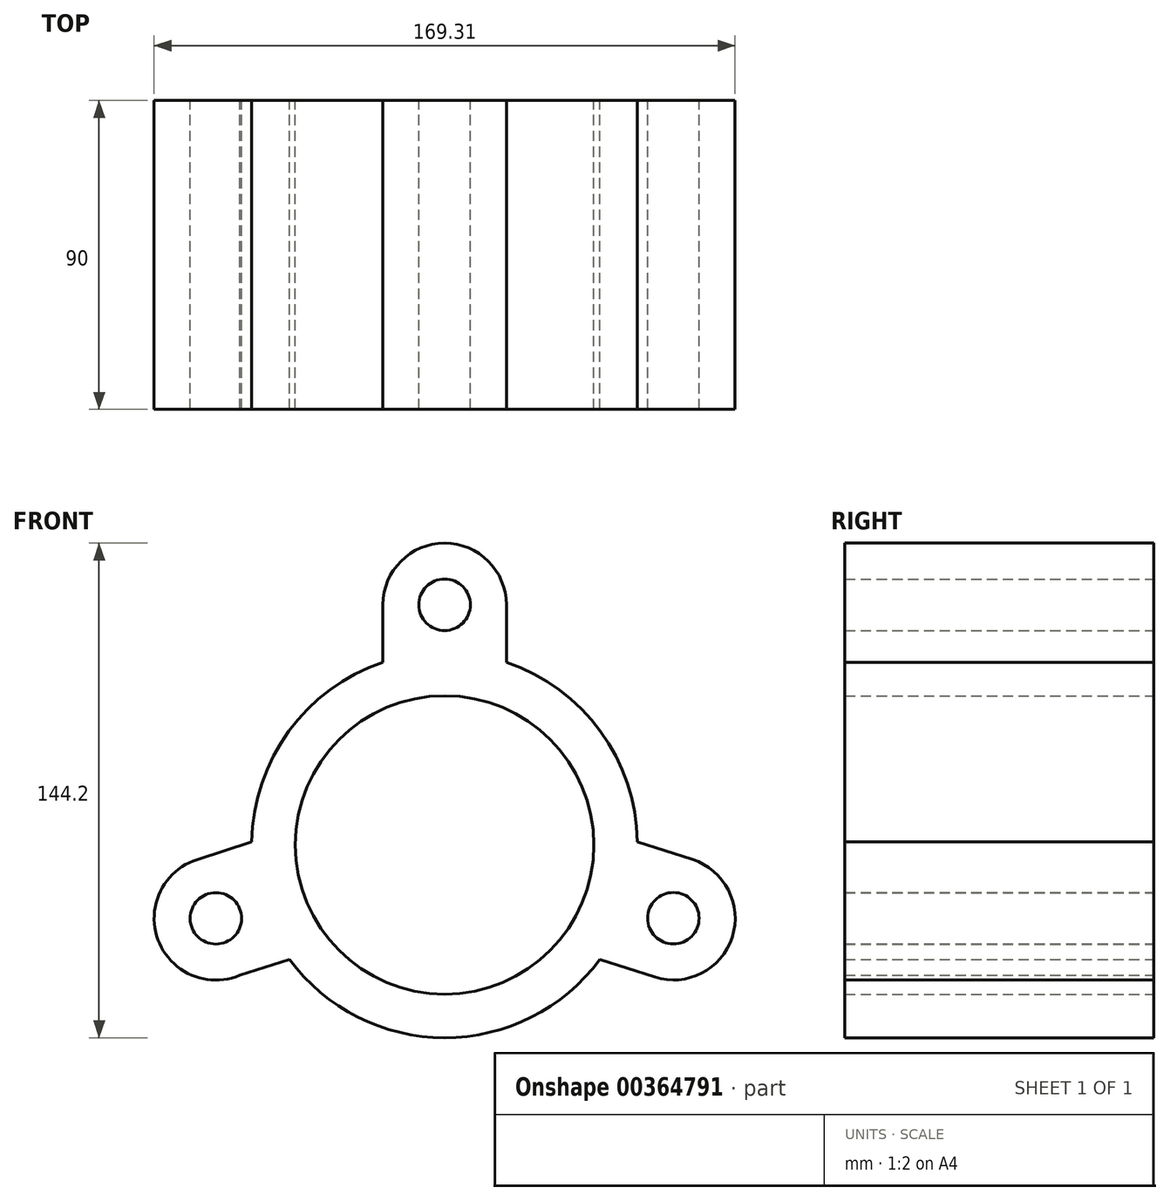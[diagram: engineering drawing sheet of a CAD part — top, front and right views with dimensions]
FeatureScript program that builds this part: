
annotation { "Feature Type Name" : "Feature", "Feature Type Description" : "" }
export const myFeature = defineFeature(function(context is Context, id is Id, definition is map)
    precondition{}
    {
        {
            var Q0;
            Q0=qCreatedBy(makeId("Front.planeOp"),FACE);
            var sketch = newSketch(context, id + "F0", { "sketchPlane" : qUnion([Q0])});
            skArc(sketch, "E0", {"start": v(-45.23, -33.36) * mm, "mid": v(-0.02, -56.2) * mm, "end": v(45.2, -33.4) * mm});
            skCircle(sketch, "E1", {"center": v(0, 0) * mm, "radius": 43.5 * mm});
            skCircle(sketch, "E2", {"center": v(0, 70) * mm, "radius": 7.5 * mm});
            skArc(sketch, "E3", {"start": v(18, 70) * mm, "mid": v(0, 88) * mm, "end": v(-18, 70) * mm});
            skLineSegment(sketch, "E4", {"start": v(-18, 70) * mm, "end": v(-18, 53.24) * mm});
            skLineSegment(sketch, "E5", {"start": v(18, 70) * mm, "end": v(18, 53.24) * mm});
            skCircle(sketch, "E6", {"center": v(-66.65, -21.4) * mm, "radius": 7.5 * mm});
            skArc(sketch, "E7", {"start": v(-72.15, -4.26) * mm, "mid": v(-83.54, -27.62) * mm, "end": v(-59.71, -38) * mm});
            skCircle(sketch, "E8", {"center": v(66.66, -21.37) * mm, "radius": 7.5 * mm});
            skArc(sketch, "E9", {"start": v(61.16, -38.5) * mm, "mid": v(83.8, -26.86) * mm, "end": v(72.15, -4.23) * mm});
            skLineSegment(sketch, "E10", {"start": v(-72.15, -4.26) * mm, "end": v(-56.2, 0.87) * mm});
            skLineSegment(sketch, "E11", {"start": v(-59.71, -38) * mm, "end": v(-45.23, -33.36) * mm});
            skLineSegment(sketch, "E12.0", {"start": v(72.15, -4.23) * mm, "end": v(56.2, 0.89) * mm});
            skLineSegment(sketch, "E13.0", {"start": v(61.16, -38.5) * mm, "end": v(45.2, -33.4) * mm});
            skArc(sketch, "E14.trimOffspring", {"start": v(-18, 53.24) * mm, "mid": v(-45.4, 33.11) * mm, "end": v(-56.2, 0.87) * mm});
            skArc(sketch, "E15.trimOffspring", {"start": v(56.2, 0.89) * mm, "mid": v(45.4, 33.12) * mm, "end": v(18, 53.24) * mm});
            skSolve(sketch);
        }
        {
            var Q0;
            Q0=makeQuery(id+"F0.imprint","IMPRINT",FACE,{"disambiguationData":[TD([[makeQuery(id+"F0.imprint","IMPRINT",EDGE,{"derivedFrom":sQuery(id+"F0.wireOp",EDGE,"E0")}),1.0]])]});
            extrude(context, id + "F1", {"entities" : qUnion([Q0]), "offsetDistance" : 25 * mm, "depth" : 90 * mm});
        }
    });
